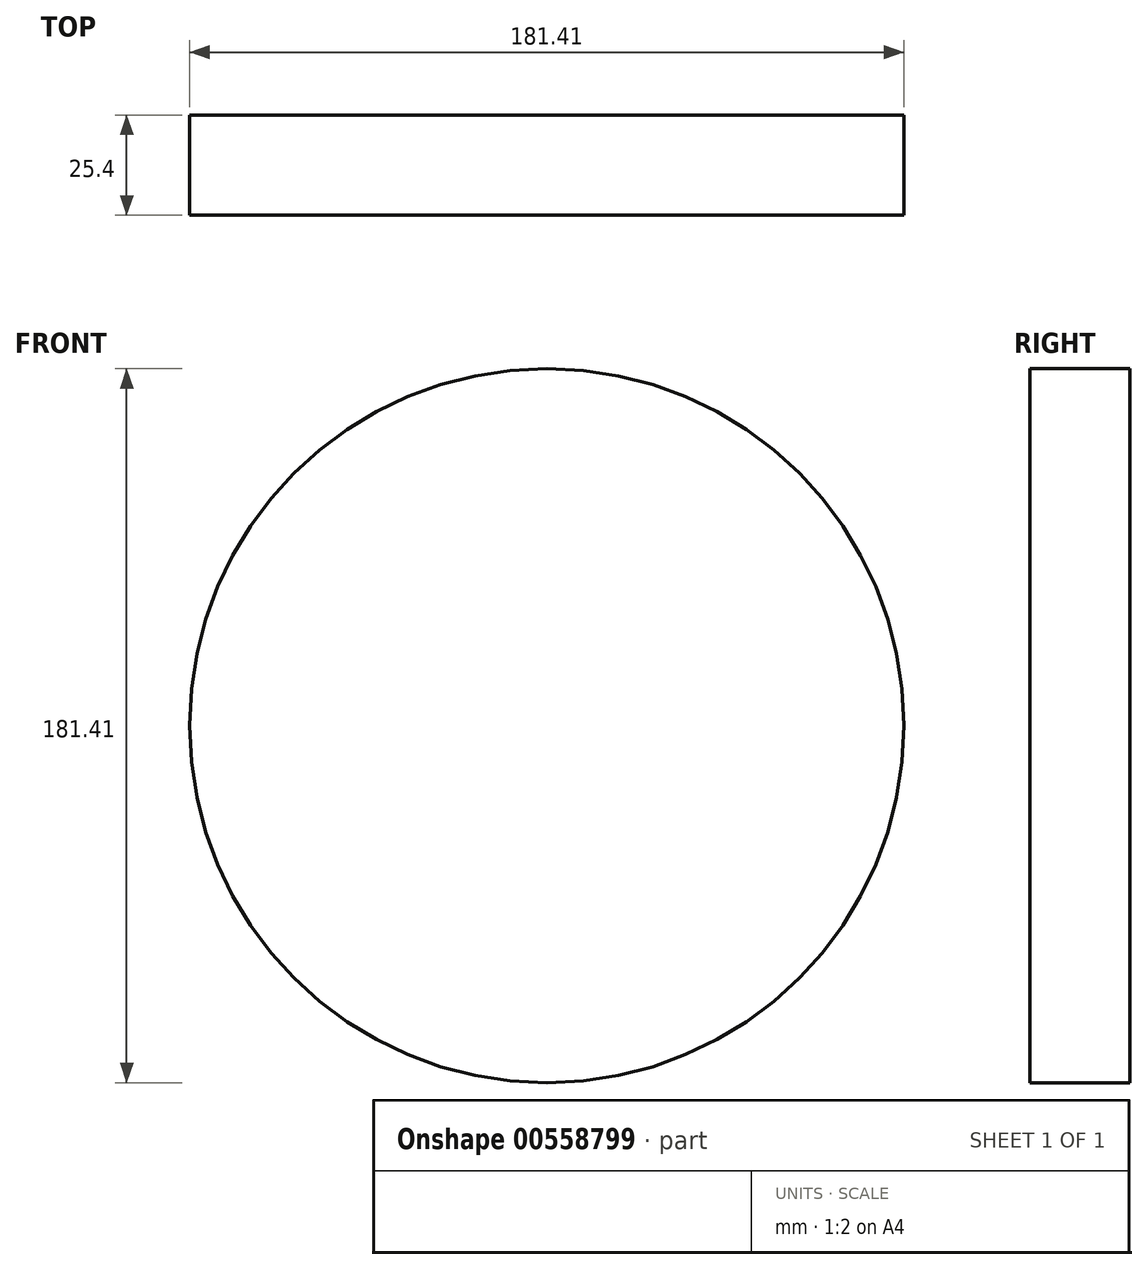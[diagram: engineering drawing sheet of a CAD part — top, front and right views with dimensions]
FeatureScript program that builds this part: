
annotation { "Feature Type Name" : "Feature", "Feature Type Description" : "" }
export const myFeature = defineFeature(function(context is Context, id is Id, definition is map)
    precondition{}
    {
        {
            var Q0;
            Q0=qCreatedBy(makeId("Front.planeOp"),FACE);
            var sketch = newSketch(context, id + "F0", { "sketchPlane" : qUnion([Q0])});
            skCircle(sketch, "E0", {"center": v(8.8, 47.82) * mm, "radius": 90.7 * mm});
            skSolve(sketch);
        }
        {
            var Q0;
            Q0 = qSketchRegion(id + "F0", true);
            extrude(context, id + "F1", {"entities" : qUnion([Q0]), "depth" : 25.4 * mm, "offsetDistance" : 25.4 * mm});
        }
    });
